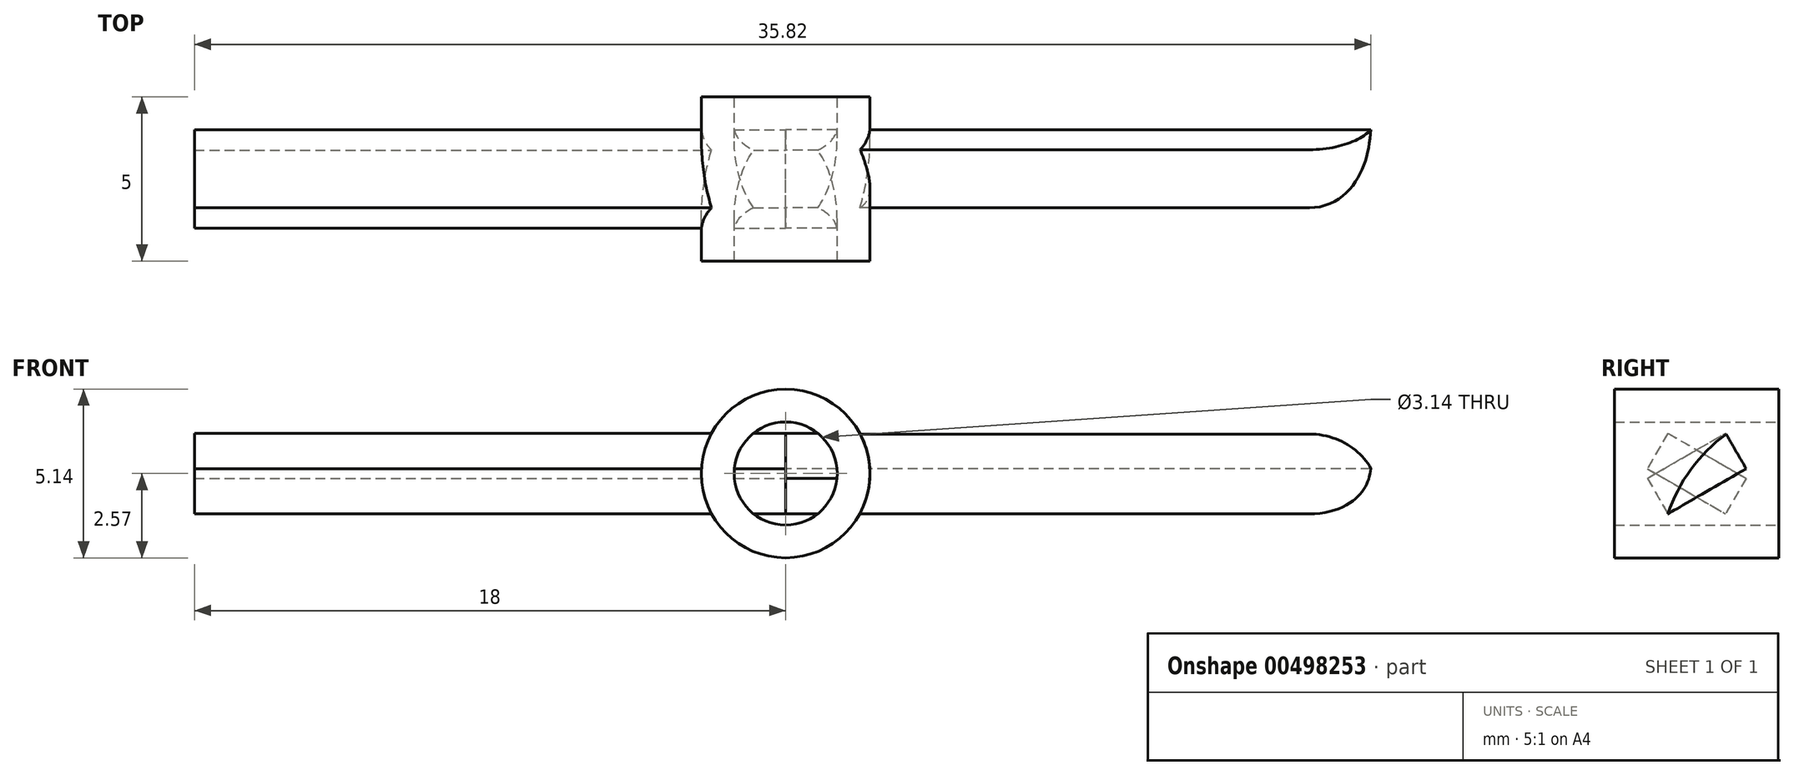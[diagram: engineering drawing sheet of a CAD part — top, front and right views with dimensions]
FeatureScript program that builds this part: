
annotation { "Feature Type Name" : "Feature", "Feature Type Description" : "" }
export const myFeature = defineFeature(function(context is Context, id is Id, definition is map)
    precondition{}
    {
        {
            var Q0;
            Q0=qCreatedBy(makeId("Front.planeOp"),FACE);
            var sketch = newSketch(context, id + "F0", { "sketchPlane" : qUnion([Q0])});
            skCircle(sketch, "E0", {"center": v(0, 0) * mm, "radius": 1.57 * mm});
            skCircle(sketch, "E1", {"center": v(0, 0) * mm, "radius": 2.57 * mm});
            skSolve(sketch);
        }
        {
            var Q0;
            Q0 = qSketchRegion(id + "F0", true);
            extrude(context, id + "F1", {"entities" : qUnion([Q0]), "depth" : 2.5 * mm});
        }
        {
            var Q0;
            Q0 = qSketchRegion(id + "F0", true);
            extrude(context, id + "F2", {"entities" : qUnion([Q0]), "operationType" : NewBodyOperationType.ADD, "oppositeDirection" : true, "depth" : 2.5 * mm});
        }
        {
            var Q0;
            Q0=qCreatedBy(makeId("Right.planeOp"),FACE);
            var sketch = newSketch(context, id + "F3", { "sketchPlane" : qUnion([Q0])});
            skLineSegment(sketch, "E2", {"start": v(-1.5, -0.15) * mm, "end": v(0.88, 1.23) * mm});
            skLineSegment(sketch, "E3", {"start": v(-1.5, -0.15) * mm, "end": v(-0.88, -1.23) * mm});
            skLineSegment(sketch, "E4", {"start": v(-0.88, -1.23) * mm, "end": v(1.5, 0.15) * mm});
            skLineSegment(sketch, "E5", {"start": v(0.88, 1.23) * mm, "end": v(1.5, 0.15) * mm});
            skSolve(sketch);
        }
        {
            var Q0;
            Q0 = qSketchRegion(id + "F3", true);
            extrude(context, id + "F4", {"entities" : qUnion([Q0]), "operationType" : NewBodyOperationType.ADD, "depth" : 18 * mm});
        }
        {
            var Q0;
            {var subQ0=sQuery(id+"F3.wireOp",EDGE,"E3");var subQ1=sQuery(id+"F3.wireOp",EDGE,"E2");var subQ2=sQuery(id+"F0.wireOp",EDGE,"E1");Q0=makeQuery(id+"F4.boolean.opBoolean","SPLIT",EDGE,{"disambiguationData":[TD([makeQuery(id+"F1.opExtrude","SWEPT_FACE",FACE,{"disambiguationData":[OSD([subQ2])]})])],"derivedFrom":makeQuery(id+"F4.opExtrude","SWEPT_EDGE",EDGE,{"disambiguationData":[OSD([subQ1,subQ0])]})});}
            fillet(context, id + "F5", {"entities" : qUnion([Q0]), "radius" : 5 * mm, "tangentPropagation" : true, "allowEdgeOverflow" : false});
        }
        {
            var Q0;
            {var subQ0=sQuery(id+"F3.wireOp",EDGE,"E3");var subQ1=sQuery(id+"F3.wireOp",EDGE,"E2");var subQ2=makeQuery(id+"F4.opExtrude","CAP_FACE",FACE,{"disambiguationData":[OSD([subQ1,subQ0,sQuery(id+"F3.wireOp",EDGE,"E4"),sQuery(id+"F3.wireOp",EDGE,"E5")])],"isStart":false});var subQ3=sQuery(id+"F0.wireOp",EDGE,"E1");Q0=makeQuery(id+"F5.opFillet","BLEND_EDGE",EDGE,{"blendedFrom":[makeQuery(id+"F4.boolean.opBoolean","SPLIT",EDGE,{"disambiguationData":[TD([makeQuery(id+"F1.opExtrude","SWEPT_FACE",FACE,{"disambiguationData":[OSD([subQ3])]})])],"derivedFrom":makeQuery(id+"F4.opExtrude","SWEPT_EDGE",EDGE,{"disambiguationData":[OSD([subQ1,subQ0])]})}),subQ2],"blendedInto":[subQ2]});}
            fillet(context, id + "F6", {"entities" : qUnion([Q0]), "radius" : 2.05 * mm, "tangentPropagation" : true, "allowEdgeOverflow" : false});
        }
        {
            var Q0;
            Q0=qCreatedBy(makeId("Right.planeOp"),FACE);
            var sketch = newSketch(context, id + "F7", { "sketchPlane" : qUnion([Q0])});
            skLineSegment(sketch, "E6", {"start": v(-0.88, 1.23) * mm, "end": v(1.5, -0.15) * mm});
            skLineSegment(sketch, "E7", {"start": v(-0.88, 1.23) * mm, "end": v(-1.5, 0.15) * mm});
            skLineSegment(sketch, "E8", {"start": v(-1.5, 0.15) * mm, "end": v(0.88, -1.23) * mm});
            skLineSegment(sketch, "E9", {"start": v(1.5, -0.15) * mm, "end": v(0.88, -1.23) * mm});
            skSolve(sketch);
        }
        {
            var Q0;
            Q0 = qSketchRegion(id + "F7", true);
            extrude(context, id + "F8", {"entities" : qUnion([Q0]), "operationType" : NewBodyOperationType.ADD, "oppositeDirection" : true, "depth" : 18 * mm});
        }
    });
